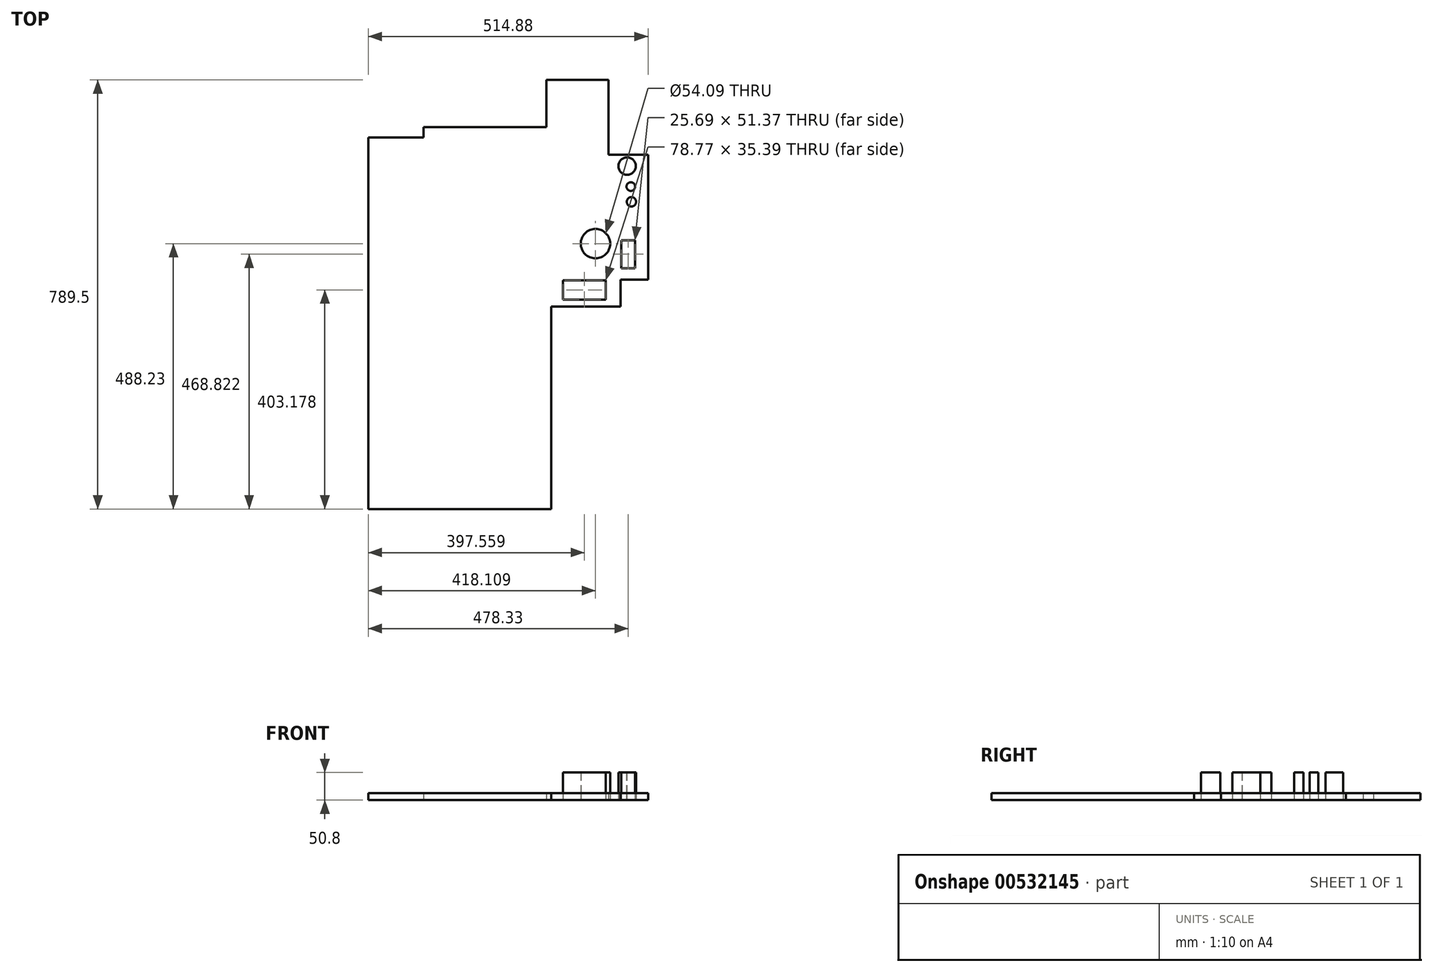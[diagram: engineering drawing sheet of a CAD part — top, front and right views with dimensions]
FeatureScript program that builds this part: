
annotation { "Feature Type Name" : "Feature", "Feature Type Description" : "" }
export const myFeature = defineFeature(function(context is Context, id is Id, definition is map)
    precondition{}
    {
        {
            var Q0;
            Q0=qCreatedBy(makeId("Top.planeOp"),FACE);
            var sketch = newSketch(context, id + "F0", { "sketchPlane" : qUnion([Q0])});
            skLineSegment(sketch, "E0", {"start": v(151.59, -45.91) * mm, "end": v(-184.96, -45.91) * mm});
            skLineSegment(sketch, "E1", {"start": v(-184.96, -45.91) * mm, "end": v(-184.96, 326.6) * mm});
            skLineSegment(sketch, "E2", {"start": v(151.59, -45.91) * mm, "end": v(151.59, 326.6) * mm});
            skLineSegment(sketch, "E3", {"start": v(151.59, 326.6) * mm, "end": v(-184.96, 326.6) * mm});
            skLineSegment(sketch, "E4", {"start": v(-184.96, 326.6) * mm, "end": v(-184.96, 637.75) * mm});
            skLineSegment(sketch, "E5", {"start": v(-184.96, 637.75) * mm, "end": v(-83.36, 637.75) * mm});
            skLineSegment(sketch, "E6", {"start": v(-83.36, 637.75) * mm, "end": v(-83.36, 656.8) * mm});
            skLineSegment(sketch, "E7", {"start": v(-83.36, 656.8) * mm, "end": v(-60.08, 656.8) * mm});
            skLineSegment(sketch, "E8", {"start": v(-60.08, 656.8) * mm, "end": v(143.12, 656.8) * mm});
            skLineSegment(sketch, "E9", {"start": v(143.12, 656.8) * mm, "end": v(143.12, 743.59) * mm});
            skLineSegment(sketch, "E10", {"start": v(143.12, 743.59) * mm, "end": v(257.42, 743.59) * mm});
            skLineSegment(sketch, "E11", {"start": v(257.42, 743.59) * mm, "end": v(257.42, 606) * mm});
            skLineSegment(sketch, "E12", {"start": v(151.59, 326.6) * mm, "end": v(151.59, 381.64) * mm});
            skLineSegment(sketch, "E13", {"start": v(151.59, 381.64) * mm, "end": v(270.77, 606) * mm});
            skLineSegment(sketch, "E14", {"start": v(151.59, 326.6) * mm, "end": v(279.18, 326.6) * mm});
            skLineSegment(sketch, "E15", {"start": v(279.18, 326.6) * mm, "end": v(279.18, 376.26) * mm});
            skLineSegment(sketch, "E16", {"start": v(279.18, 376.26) * mm, "end": v(329.92, 376.26) * mm});
            skLineSegment(sketch, "E17", {"start": v(329.92, 376.26) * mm, "end": v(329.92, 606) * mm});
            skLineSegment(sketch, "E18", {"start": v(329.92, 606) * mm, "end": v(270.77, 606) * mm});
            skLineSegment(sketch, "E19", {"start": v(257.42, 606) * mm, "end": v(270.77, 606) * mm});
            skLineSegment(sketch, "E20", {"start": v(173.21, 339.57) * mm, "end": v(173.21, 374.96) * mm});
            skLineSegment(sketch, "E21", {"start": v(173.21, 374.96) * mm, "end": v(251.99, 374.96) * mm});
            skLineSegment(sketch, "E22", {"start": v(251.99, 374.96) * mm, "end": v(251.99, 339.57) * mm});
            skLineSegment(sketch, "E23", {"start": v(251.99, 339.57) * mm, "end": v(173.21, 339.57) * mm});
            skLineSegment(sketch, "E24", {"start": v(280.53, 397.22) * mm, "end": v(306.21, 397.22) * mm});
            skLineSegment(sketch, "E25", {"start": v(306.21, 397.22) * mm, "end": v(306.21, 448.6) * mm});
            skLineSegment(sketch, "E26", {"start": v(306.21, 448.6) * mm, "end": v(280.53, 448.6) * mm});
            skLineSegment(sketch, "E27", {"start": v(280.53, 448.6) * mm, "end": v(280.53, 397.22) * mm});
            skCircle(sketch, "E28", {"center": v(291.37, 585.02) * mm, "radius": 16.02 * mm});
            skCircle(sketch, "E29", {"center": v(298.22, 547.35) * mm, "radius": 8 * mm});
            skCircle(sketch, "E30", {"center": v(299.36, 519.38) * mm, "radius": 8.58 * mm});
            skCircle(sketch, "E31", {"center": v(233.15, 442.32) * mm, "radius": 27.05 * mm});
            skSolve(sketch);
        }
        {
            var Q0;
            Q0=makeQuery(id+"F0.imprint","IMPRINT",FACE,{"disambiguationData":[TD([[makeQuery(id+"F0.imprint","IMPRINT",EDGE,{"derivedFrom":sQuery(id+"F0.wireOp",EDGE,"E31")}),1.0]])]});
            extrude(context, id + "F1", {"entities" : qUnion([Q0]), "depth" : 50.8 * mm, "offsetDistance" : 25.4 * mm});
        }
        {
            var Q0;
            Q0=makeQuery(id+"F0.imprint","IMPRINT",FACE,{"disambiguationData":[TD([[makeQuery(id+"F0.imprint","IMPRINT",EDGE,{"derivedFrom":sQuery(id+"F0.wireOp",EDGE,"E24")}),1.0]])]});
            extrude(context, id + "F2", {"entities" : qUnion([Q0]), "depth" : 50.8 * mm, "offsetDistance" : 25.4 * mm});
        }
        {
            var Q0;
            Q0=makeQuery(id+"F0.imprint","IMPRINT",FACE,{"disambiguationData":[TD([[makeQuery(id+"F0.imprint","IMPRINT",EDGE,{"derivedFrom":sQuery(id+"F0.wireOp",EDGE,"E20")}),-1.0]])]});
            extrude(context, id + "F3", {"entities" : qUnion([Q0]), "depth" : 50.8 * mm, "offsetDistance" : 25.4 * mm});
        }
        {
            var Q0;
            Q0=makeQuery(id+"F0.imprint","IMPRINT",FACE,{"disambiguationData":[TD([[makeQuery(id+"F0.imprint","IMPRINT",EDGE,{"derivedFrom":sQuery(id+"F0.wireOp",EDGE,"E30")}),1.0]])]});
            var Q1;
            Q1=makeQuery(id+"F0.imprint","IMPRINT",FACE,{"disambiguationData":[TD([[makeQuery(id+"F0.imprint","IMPRINT",EDGE,{"derivedFrom":sQuery(id+"F0.wireOp",EDGE,"E28")}),1.0]])]});
            var Q2;
            Q2=makeQuery(id+"F0.imprint","IMPRINT",FACE,{"disambiguationData":[TD([[makeQuery(id+"F0.imprint","IMPRINT",EDGE,{"derivedFrom":sQuery(id+"F0.wireOp",EDGE,"E29")}),1.0]])]});
            extrude(context, id + "F4", {"entities" : qUnion([Q0, Q1, Q2]), "depth" : 50.8 * mm, "offsetDistance" : 25.4 * mm});
        }
        {
            var Q0;
            Q0=makeQuery(id+"F0.imprint","IMPRINT",FACE,{"disambiguationData":[TD([[makeQuery(id+"F0.imprint","IMPRINT",EDGE,{"derivedFrom":sQuery(id+"F0.wireOp",EDGE,"E3")}),-1.0]])]});
            var Q1;
            Q1=makeQuery(id+"F0.imprint","IMPRINT",FACE,{"disambiguationData":[TD([[makeQuery(id+"F0.imprint","IMPRINT",EDGE,{"derivedFrom":sQuery(id+"F0.wireOp",EDGE,"E0")}),-1.0]])]});
            var Q2;
            Q2=makeQuery(id+"F0.imprint","IMPRINT",FACE,{"disambiguationData":[TD([[makeQuery(id+"F0.imprint","IMPRINT",EDGE,{"derivedFrom":sQuery(id+"F0.wireOp",EDGE,"E12")}),-1.0]])]});
            extrude(context, id + "F5", {"entities" : qUnion([Q0, Q1, Q2]), "depth" : 12.7 * mm, "offsetDistance" : 25.4 * mm});
        }
    });
